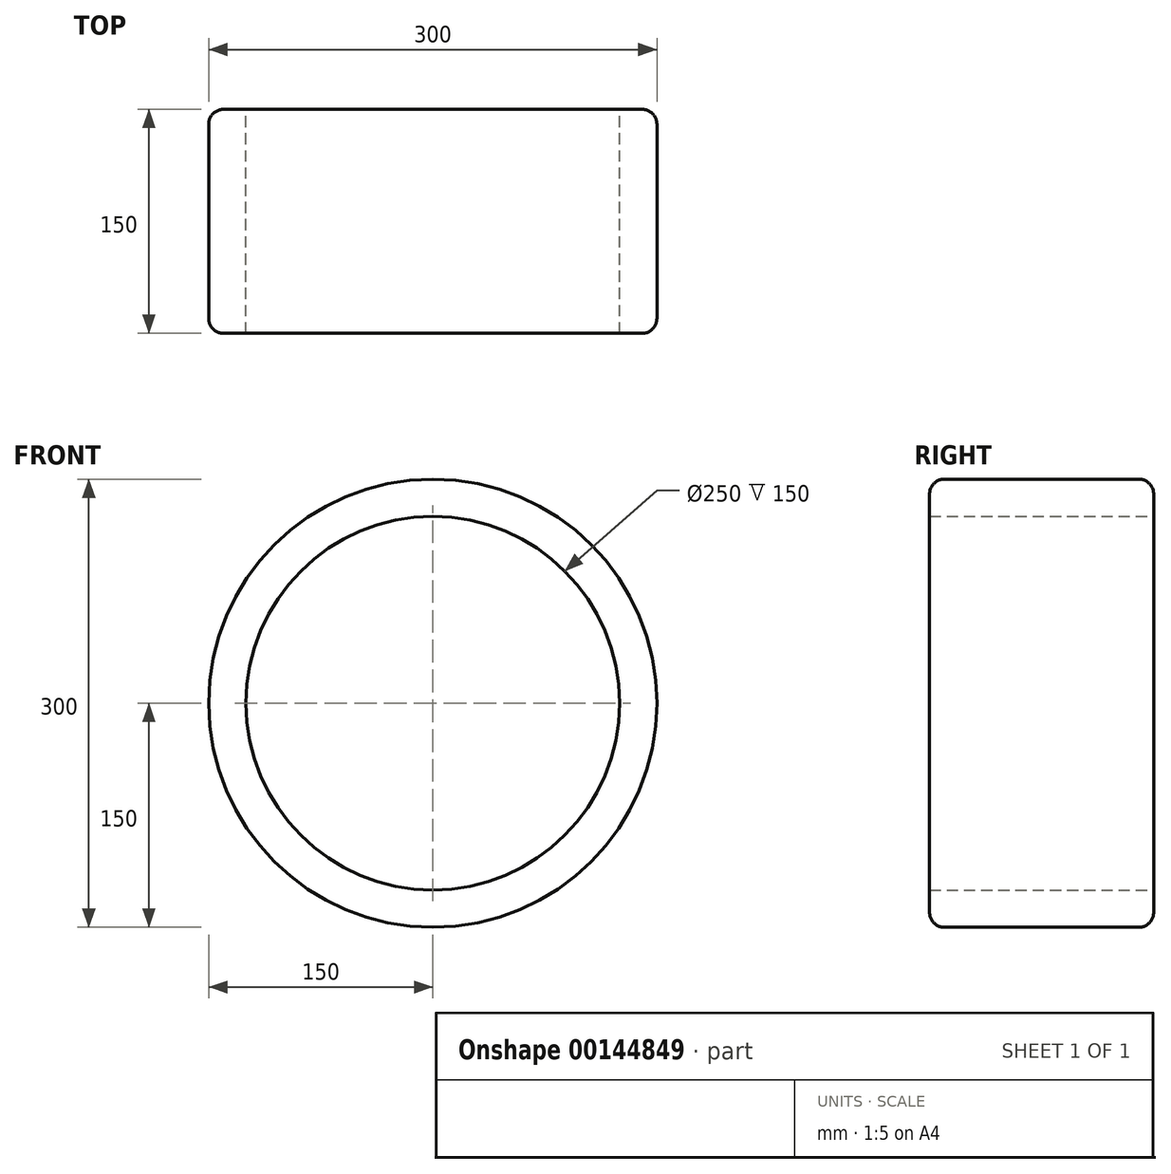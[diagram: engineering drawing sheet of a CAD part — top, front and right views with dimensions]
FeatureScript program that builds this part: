
annotation { "Feature Type Name" : "Feature", "Feature Type Description" : "" }
export const myFeature = defineFeature(function(context is Context, id is Id, definition is map)
    precondition{}
    {
        {
            var Q0;
            Q0=qCreatedBy(makeId("Front.planeOp"),FACE);
            var sketch = newSketch(context, id + "F0", { "sketchPlane" : qUnion([Q0])});
            skCircle(sketch, "E0", {"center": v(0, 0) * mm, "radius": 125 * mm});
            skCircle(sketch, "E1", {"center": v(0, 0) * mm, "radius": 150 * mm});
            skSolve(sketch);
        }
        {
            var Q0;
            Q0=makeQuery(id+"F0.imprint","IMPRINT",FACE,{"disambiguationData":[TD([[makeQuery(id+"F0.imprint","IMPRINT",EDGE,{"derivedFrom":sQuery(id+"F0.wireOp",EDGE,"E0")}),-1.0]])]});
            extrude(context, id + "F1", {"entities" : qUnion([Q0]), "depth" : 150 * mm});
        }
        {
            var Q0;
            Q0=makeQuery(id+"F1.opExtrude","CAP_EDGE",EDGE,{"disambiguationData":[OSD([sQuery(id+"F0.wireOp",EDGE,"E1")])],"isStart":true});
            var Q1;
            Q1=makeQuery(id+"F1.opExtrude","CAP_EDGE",EDGE,{"disambiguationData":[OSD([sQuery(id+"F0.wireOp",EDGE,"E1")])],"isStart":false});
            fillet(context, id + "F2", {"entities" : qUnion([Q0, Q1]), "radius" : 10 * mm, "tangentPropagation" : true, "allowEdgeOverflow" : false});
        }
    });
